# Revit family: 51682281
name_source: partatom
category: Plumbing Fixtures
revit_build: Autodesk Revit 2016 (Build: 20150714_1515(x64)
units: mm (PartAtom-declared; Revit-internal decimal feet)

## family parameters
Always vertical = Yes
Cut with Voids When Loaded = No
OmniClass Number = 23.45.55.00
OmniClass Title = Sanitary Faucets, Wastes
Part Type = Normal
Room Calculation Point = No
Round Connector Dimension = Use Diameter
Shared = No
Work Plane-Based = No

## types (1)
- 51682281 Washbasin faucet, 3 V
    2D/3D/BIM Files URL = http://static.hansa.com
    Advanced Features = Without draw-rod opening;3S-Installation
    Aerator = Pressure controlled aerator;HONEYCOMB;CACHE integrated aerator
    AssetType = Fixed
    BIMObjectName = 51682281
    Battery = AA 1.5 V Lithium x 2, CR 2450 3 V
    BodyMaterial = Brass
    Brand = Hansa
    Catalog Drawing URL = http://static.hansa.com
    Category = Bathroom
    Class = Single lever
    CloseOffRating = 0
    Color = Chrome
    Connection Size = G3/8
    ConvergoRefNr = 0087-1806-0118-FI
    Customs Code = 84818011
    DN Size = DN15
    Dimension Drawing URL = http://static.hansa.com
    Diverter = Integrated diverter / automatic reset
    DurationUnit = Year
    EAN Number = 4057304006340
    EMC Directive = 2014/30/EU
    EN Standard = EN 15091 , EN 817
    Electronic Parts = Control unit
    Extensions = No pop-up waste included
    FDV Document URL = http://www.hansa.com
    FaucetMainMaterial = Brass
    FaucetNominalDepth = 158 mm
    FaucetNominalHeight = 170 mm  [stored 0.557743 ft]
    FaucetNominalWidth = 49 mm  [stored 0.160761 ft]
    Features = Single lever
    Finish = Polished
    Flow Drawing URL = http://static.hansa.com
    Flow Rate At 300kPa With Flow Controller = 0.1 L/s
    FlowCoefficient = 0
    Group = Washbasin faucets
    Hand Shower = Remote operated Smart Bidetta
    HandShowerNominalDepth = 69 mm
    HandShowerNominalHeight = 368 mm
    HandShowerNominalWidth = 57 mm  [stored 0.187008 ft]
    IfcExportAs = IfcValveType
    IfcExportType = FAUCET
    InletConnectionSize = 10 mm  [stored 0.0328084 ft]
    Installation Type = Deck mounted
    Installation and Maintenance = http://static.hansa.com
    Lever Handle = Lever with H+C symbol
    Long Marketing = with remotely operated function handshower
    ManufacterURL = www.hansa.com
    Manufacturer = Hansa
    ManufacturerName = Hansa
    Market = AUT;BEL;DEU;ESP;INT;NLD
    Material = Brass
    Max Flow Period = 120.0 s
    Max. Hot Water Supply = 70 °C
    Model = 51682281 Washbasin faucet, 3 V
    ModelReference = 51682281
    Mounting Holes = 1 mounting hole
    NBSDescription = Water supply fittings for washbasins and troughs
    NBSReference = 45-35-70/371
    Name = 51682281 Washbasin faucet, 3 V
    Name_en = 51682281 Washbasin faucet, 3 V
    Noise Class = I (ISO 3822)
    Operating Voltage = 3 V
    Package Weight = 4.336 kg
    Package external Dimensions = 589 x 181 x 112
    Pipes = Flexible inlet pipes
    Pressure Loss With Flow 01ls = 100000.0 Pa
    Product Code = 51682281
    Product Datasheet = http://www.hansa.com
    Product Family = HANSADESIGNO Style
    Product Image URL = http://static.hansa.com
    Product URL = http://static.hansa.com
    Projection = 119 mm  [stored 0.39042 ft]
    Protection Class = IP 55
    Revision = 2
    Shape = Sculptured
    Short Marketing = one-hole single-lever basin mixer, DN 15
    Shower Parts = Shower Hose (1500 mm);Shower holder
    Size = Faucet:49x158x170 mm / Hand shower: 57x69x368 mm
    Spare Parts = http://static.hansa.com
    Spout Type = Fixed spout
    Temperature = Thermostatic temperature control;Thermostatic safety stop at 38°C
    Uniclass2 = Pr_40_30_96_96
    Uniclass2015Description = Washbasin manual water supply sets
    Uniclass2015Reference = Pr_40_20_87_96
    Version = 2
    VersionDate = 01/01/2019
    WarrantyDescription = http://warranty.hansa.com
    WarrantyDurationUnit = Year
    WorkingPressure = 100 - 1000 kPa

note: [stored X ft] marks values corroborated as IEEE doubles in the binary element streams (Revit-internal decimal feet)

## geometry (parser evidence)
native form markers: Sweep x10
no freeform markers — native parametric forms only
